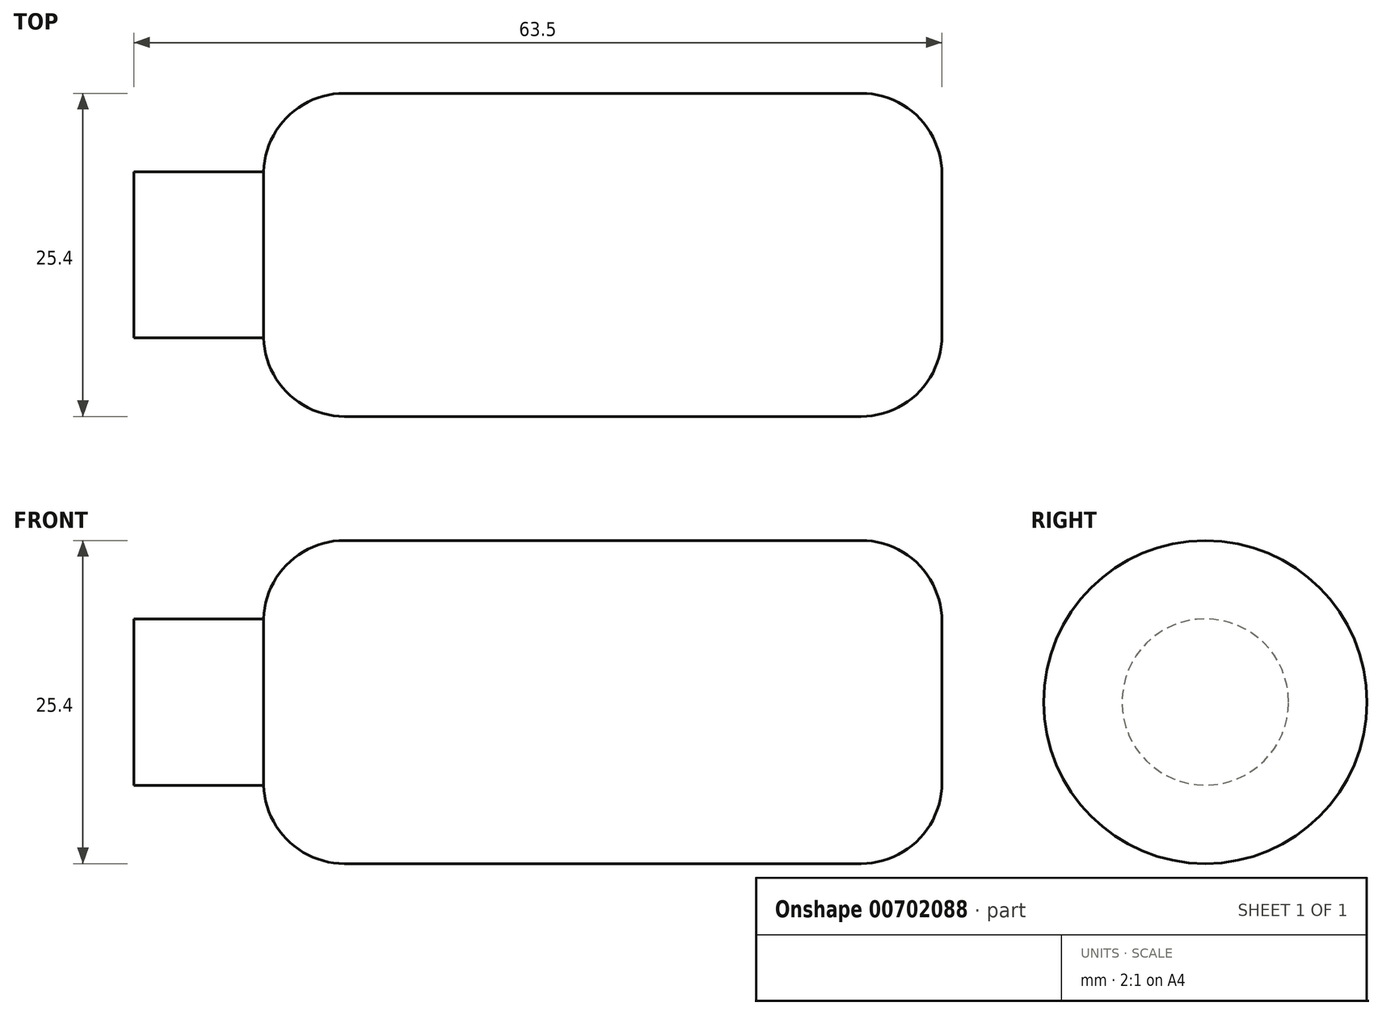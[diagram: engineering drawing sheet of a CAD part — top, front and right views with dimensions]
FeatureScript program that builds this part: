
annotation { "Feature Type Name" : "Feature", "Feature Type Description" : "" }
export const myFeature = defineFeature(function(context is Context, id is Id, definition is map)
    precondition{}
    {
        {
            var Q0;
            Q0=qCreatedBy(makeId("Front.planeOp"),FACE);
            var sketch = newSketch(context, id + "F0", { "sketchPlane" : qUnion([Q0])});
            skLineSegment(sketch, "E0", {"start": v(0, 0) * mm, "end": v(-63.5, 0) * mm});
            skLineSegment(sketch, "E1", {"start": v(-63.5, 0) * mm, "end": v(-63.5, 6.54) * mm});
            skLineSegment(sketch, "E2", {"start": v(-63.5, 6.54) * mm, "end": v(-53.3, 6.54) * mm});
            skLineSegment(sketch, "E3", {"start": v(-53.3, 6.54) * mm, "end": v(-53.3, 12.7) * mm});
            skLineSegment(sketch, "E4", {"start": v(-53.3, 12.7) * mm, "end": v(0, 12.7) * mm});
            skLineSegment(sketch, "E5", {"start": v(0, 0) * mm, "end": v(0, 12.7) * mm});
            skSolve(sketch);
        }
        {
            var Q0;
            Q0=makeQuery(id+"F0.imprint","IMPRINT",FACE,{"disambiguationData":[TD([[makeQuery(id+"F0.imprint","IMPRINT",EDGE,{"derivedFrom":sQuery(id+"F0.wireOp",EDGE,"E0")}),-1.0]])]});
            var Q1;
            Q1=sQuery(id+"F0.wireOp",EDGE,"E0");
            revolve(context, id + "F1", {"entities" : qUnion([Q0]), "axis" : qUnion([Q1]), "revolveType" : RevolveType.FULL, "surfaceOperationType" : NewSurfaceOperationType.NEW});
        }
        {
            var Q0;
            Q0=makeQuery(id+"F1.opRevolve","SWEPT_EDGE",EDGE,{"disambiguationData":[OSD([sQuery(id+"F0.wireOp",EDGE,"E4"),sQuery(id+"F0.wireOp",EDGE,"E5")])]});
            fillet(context, id + "F2", {"entities" : qUnion([Q0]), "radius" : 6.35 * mm, "tangentPropagation" : true, "allowEdgeOverflow" : false});
        }
        {
            var Q0;
            Q0=makeQuery(id+"F1.opRevolve","SWEPT_EDGE",EDGE,{"disambiguationData":[OSD([sQuery(id+"F0.wireOp",EDGE,"E3"),sQuery(id+"F0.wireOp",EDGE,"E4")])]});
            fillet(context, id + "F3", {"entities" : qUnion([Q0]), "radius" : 6.35 * mm, "tangentPropagation" : true, "allowEdgeOverflow" : false});
        }
    });
